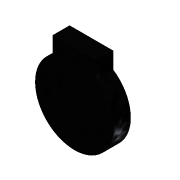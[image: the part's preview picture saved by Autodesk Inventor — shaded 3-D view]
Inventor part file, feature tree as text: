
AUTODESK INVENTOR PART (.ipt)
format: ipt  version: 2016 (Build 200138000, 138)  size: 94,208 bytes
history: native  units: mm
features: extrude x3, sketch x3
ambient origin geometry x8: Origin, YZ Plane, XZ Plane, XY Plane, X Axis, Y Axis, Z Axis, Center Point
bodies: Solid1 (feature_tree)
feature tree (6):
  extrude  "Extrusion1"  Depth=12.0mm TaperAngle=0.0deg
  extrude  "Extrusion2"  Depth=31.0mm
  extrude  "Extrusion3"  Depth=10.0mm
  sketch  "Sketch1"  dims[d0=56.0mm d1=12.0mm d2=0.0mm]
  sketch  "Sketch3"  dims[d5=15.5mm d6=31.0mm]
  sketch  "Sketch4"  dims[d7=35.0mm d8=0.0mm d9=6.0mm d10=10.0mm d11=0.0mm]
